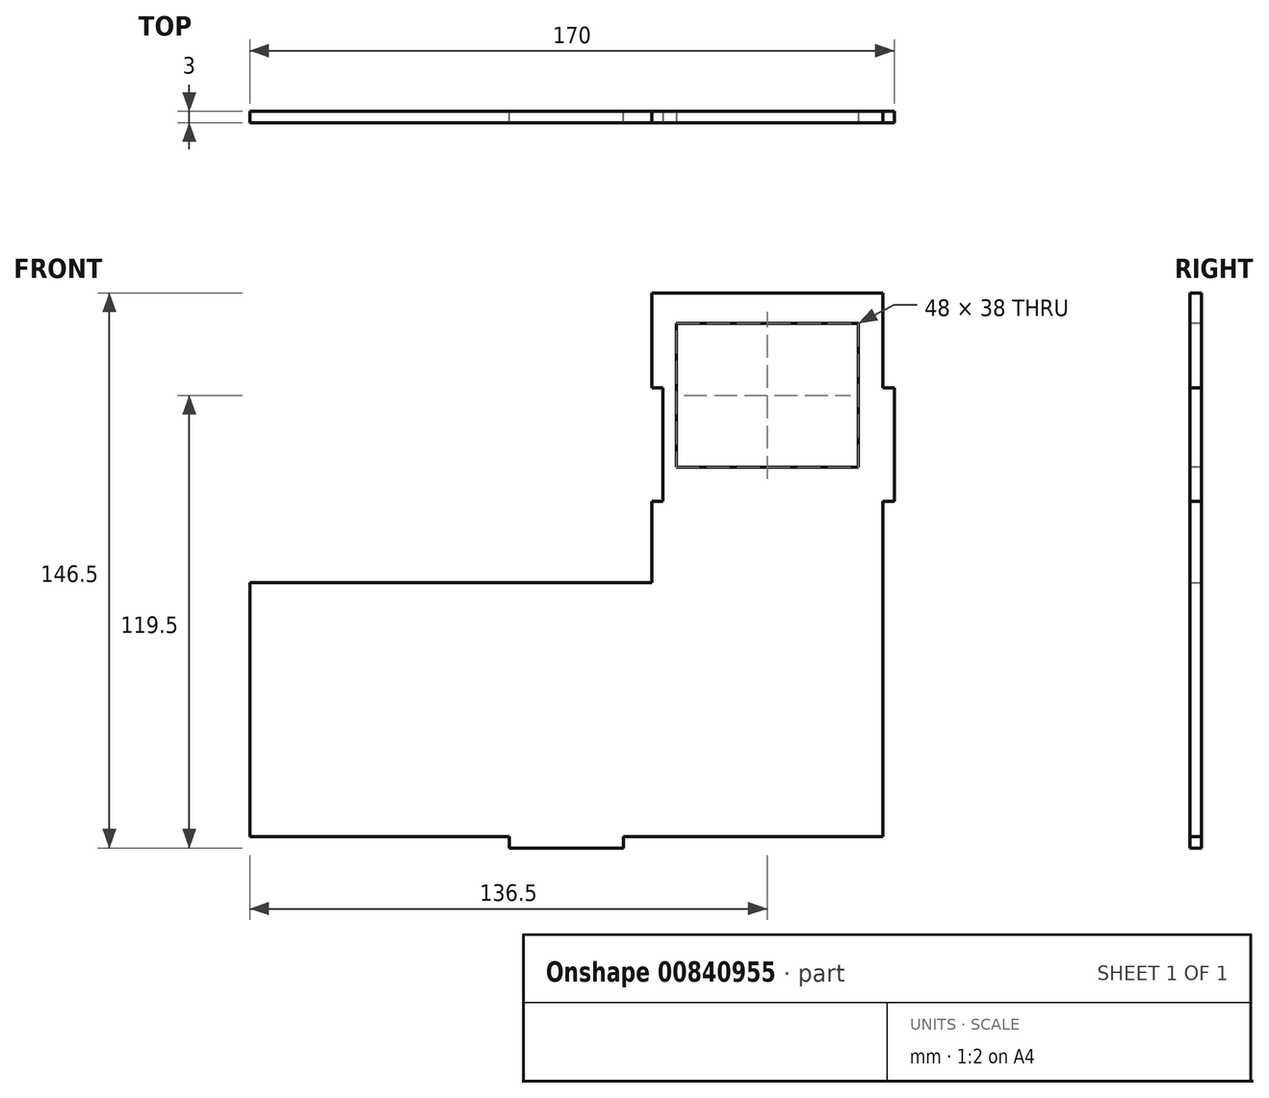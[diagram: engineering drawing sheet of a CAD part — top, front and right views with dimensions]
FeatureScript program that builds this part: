
annotation { "Feature Type Name" : "Feature", "Feature Type Description" : "" }
export const myFeature = defineFeature(function(context is Context, id is Id, definition is map)
    precondition{}
    {
        {
            var Q0;
            Q0=qCreatedBy(makeId("Front.planeOp"),FACE);
            var sketch = newSketch(context, id + "F0", { "sketchPlane" : qUnion([Q0])});
            skLineSegment(sketch, "E0.bottom", {"start": v(0, 0) * mm, "end": v(167, 0) * mm});
            skLineSegment(sketch, "E1", {"start": v(167, 0) * mm, "end": v(167, 143.5) * mm});
            skLineSegment(sketch, "E2", {"start": v(167, 143.5) * mm, "end": v(106, 143.5) * mm});
            skLineSegment(sketch, "E3", {"start": v(106, 143.5) * mm, "end": v(106, 67) * mm});
            skLineSegment(sketch, "E4", {"start": v(106, 67) * mm, "end": v(0, 67) * mm});
            skLineSegment(sketch, "E5", {"start": v(0, 67) * mm, "end": v(0, 0) * mm});
            skLineSegment(sketch, "E6", {"start": v(83.5, 0) * mm, "end": v(83.5, 56.4) * mm, "construction": true});
            skLineSegment(sketch, "E7.bottom", {"start": v(68.5, 0) * mm, "end": v(98.5, 0) * mm});
            skLineSegment(sketch, "E7.top", {"start": v(68.5, -3) * mm, "end": v(98.5, -3) * mm});
            skLineSegment(sketch, "E7.left", {"start": v(68.5, 0) * mm, "end": v(68.5, -3) * mm});
            skLineSegment(sketch, "E7.right", {"start": v(98.5, 0) * mm, "end": v(98.5, -3) * mm});
            skLineSegment(sketch, "E8.bottom", {"start": v(167, 118.5) * mm, "end": v(170, 118.5) * mm});
            skLineSegment(sketch, "E8.top", {"start": v(167, 88.5) * mm, "end": v(170, 88.5) * mm});
            skLineSegment(sketch, "E8.left", {"start": v(167, 118.5) * mm, "end": v(167, 88.5) * mm});
            skLineSegment(sketch, "E8.right", {"start": v(170, 118.5) * mm, "end": v(170, 88.5) * mm});
            skSolve(sketch);
        }
        {
            var Q0;
            Q0 = qSketchRegion(id + "F0", true);
            extrude(context, id + "F1", {"entities" : qUnion([Q0]), "depth" : 3 * mm, "offsetDistance" : 25 * mm});
        }
        {
            var Q0;
            Q0=makeQuery(id+"F1.opExtrude","CAP_FACE",FACE,{"disambiguationData":[OSD([sQuery(id+"F0.wireOp",EDGE,"E0.bottom"),sQuery(id+"F0.wireOp",EDGE,"E1"),sQuery(id+"F0.wireOp",EDGE,"E2"),sQuery(id+"F0.wireOp",EDGE,"E3"),sQuery(id+"F0.wireOp",EDGE,"E4"),sQuery(id+"F0.wireOp",EDGE,"E5")])],"isStart":false});
            var sketch = newSketch(context, id + "F2", { "sketchPlane" : qUnion([Q0])});
            skLineSegment(sketch, "E9.bottom", {"start": v(112.5, 135.5) * mm, "end": v(160.5, 135.5) * mm});
            skLineSegment(sketch, "E9.top", {"start": v(112.5, 97.5) * mm, "end": v(160.5, 97.5) * mm});
            skLineSegment(sketch, "E9.left", {"start": v(112.5, 135.5) * mm, "end": v(112.5, 97.5) * mm});
            skLineSegment(sketch, "E9.right", {"start": v(160.5, 135.5) * mm, "end": v(160.5, 97.5) * mm});
            skLineSegment(sketch, "E10.bottom", {"start": v(106, 118.5) * mm, "end": v(109, 118.5) * mm});
            skLineSegment(sketch, "E10.top", {"start": v(106, 88.5) * mm, "end": v(109, 88.5) * mm});
            skLineSegment(sketch, "E10.left", {"start": v(106, 118.5) * mm, "end": v(106, 88.5) * mm});
            skLineSegment(sketch, "E10.right", {"start": v(109, 118.5) * mm, "end": v(109, 88.5) * mm});
            skSolve(sketch);
        }
        {
            var Q0;
            Q0 = qSketchRegion(id + "F2", true);
            extrude(context, id + "F3", {"entities" : qUnion([Q0]), "operationType" : NewBodyOperationType.REMOVE, "oppositeDirection" : true, "depth" : 25 * mm, "offsetDistance" : 25 * mm});
        }
    });
